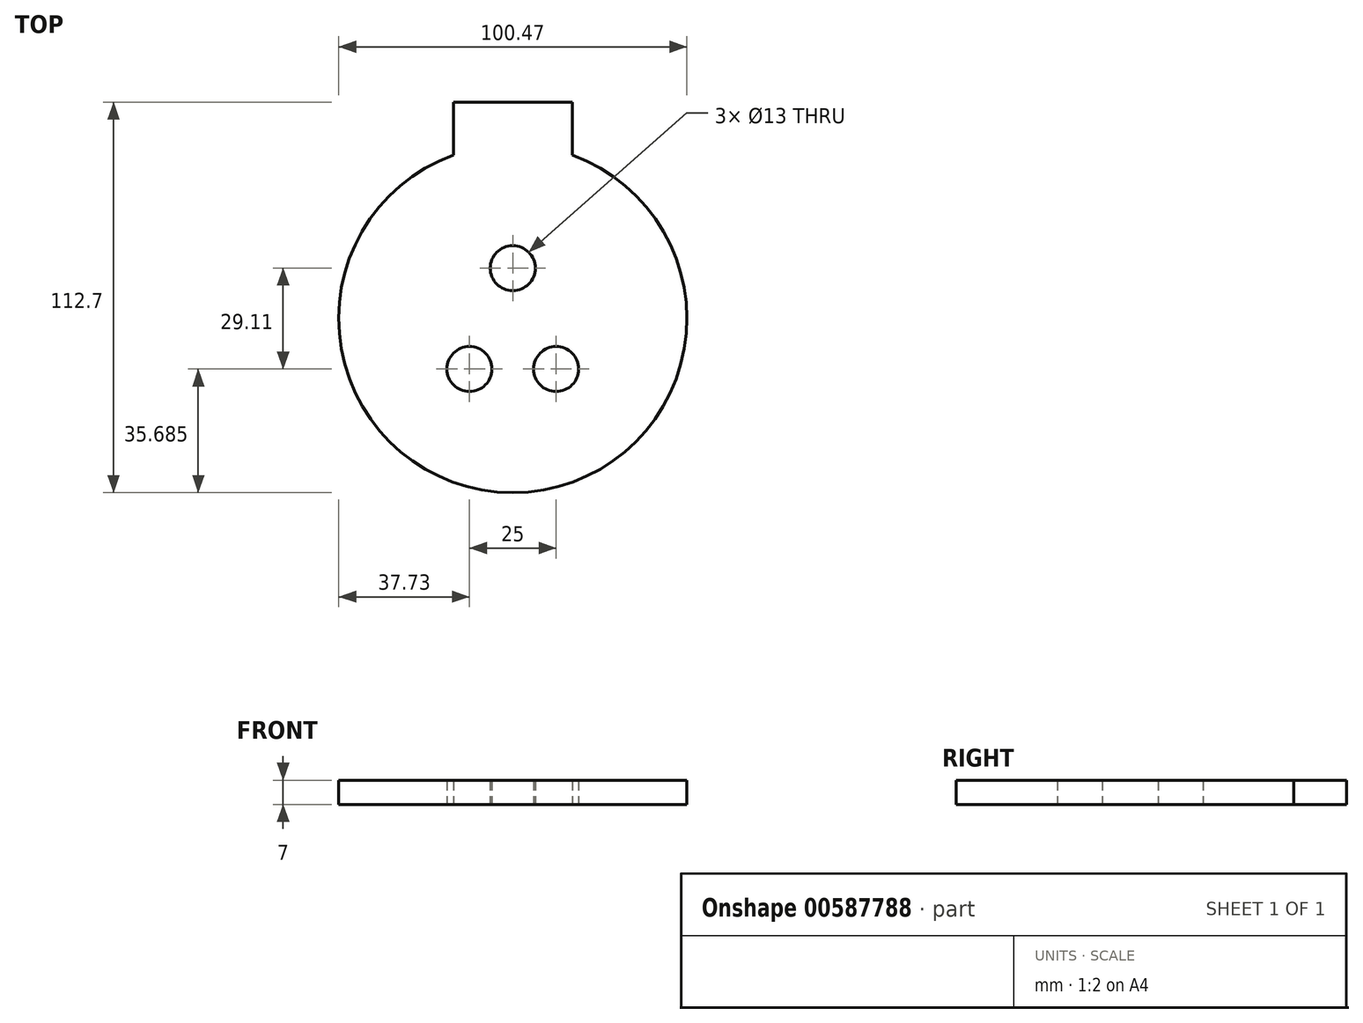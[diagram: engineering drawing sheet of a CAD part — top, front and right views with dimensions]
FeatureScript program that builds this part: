
annotation { "Feature Type Name" : "Feature", "Feature Type Description" : "" }
export const myFeature = defineFeature(function(context is Context, id is Id, definition is map)
    precondition{}
    {
        {
            var Q0;
            Q0=qCreatedBy(makeId("Top.planeOp"),FACE);
            var sketch = newSketch(context, id + "F0", { "sketchPlane" : qUnion([Q0])});
            skCircle(sketch, "E0", {"center": v(0, 14.55) * mm, "radius": 6.5 * mm});
            skCircle(sketch, "E1", {"center": v(12.5, -14.55) * mm, "radius": 6.5 * mm});
            skCircle(sketch, "E2.MirrorC", {"center": v(-12.5, -14.55) * mm, "radius": 6.5 * mm});
            skArc(sketch, "E3", {"start": v(-17.15, 47.22) * mm, "mid": v(0, -50.24) * mm, "end": v(17.15, 47.22) * mm});
            skLineSegment(sketch, "E4", {"start": v(0, 62.46) * mm, "end": v(17.15, 62.46) * mm});
            skLineSegment(sketch, "E5", {"start": v(17.15, 62.46) * mm, "end": v(17.15, 47.22) * mm});
            skLineSegment(sketch, "E6.MirrorCS", {"start": v(0, 62.46) * mm, "end": v(-17.15, 62.46) * mm});
            skLineSegment(sketch, "E7.MirrorCS", {"start": v(-17.15, 62.46) * mm, "end": v(-17.15, 47.22) * mm});
            skPoint(sketch, "E8.start.orphan", {"position": v(0, 50.23) * mm});
            skSolve(sketch);
        }
        {
            var Q0;
            Q0=makeQuery(id+"F0.imprint","IMPRINT",FACE,{"disambiguationData":[TD([[makeQuery(id+"F0.imprint","IMPRINT",EDGE,{"derivedFrom":sQuery(id+"F0.wireOp",EDGE,"E0")}),-1.0]])]});
            extrude(context, id + "F1", {"entities" : qUnion([Q0]), "depth" : 7 * mm, "offsetDistance" : 25 * mm});
        }
    });
